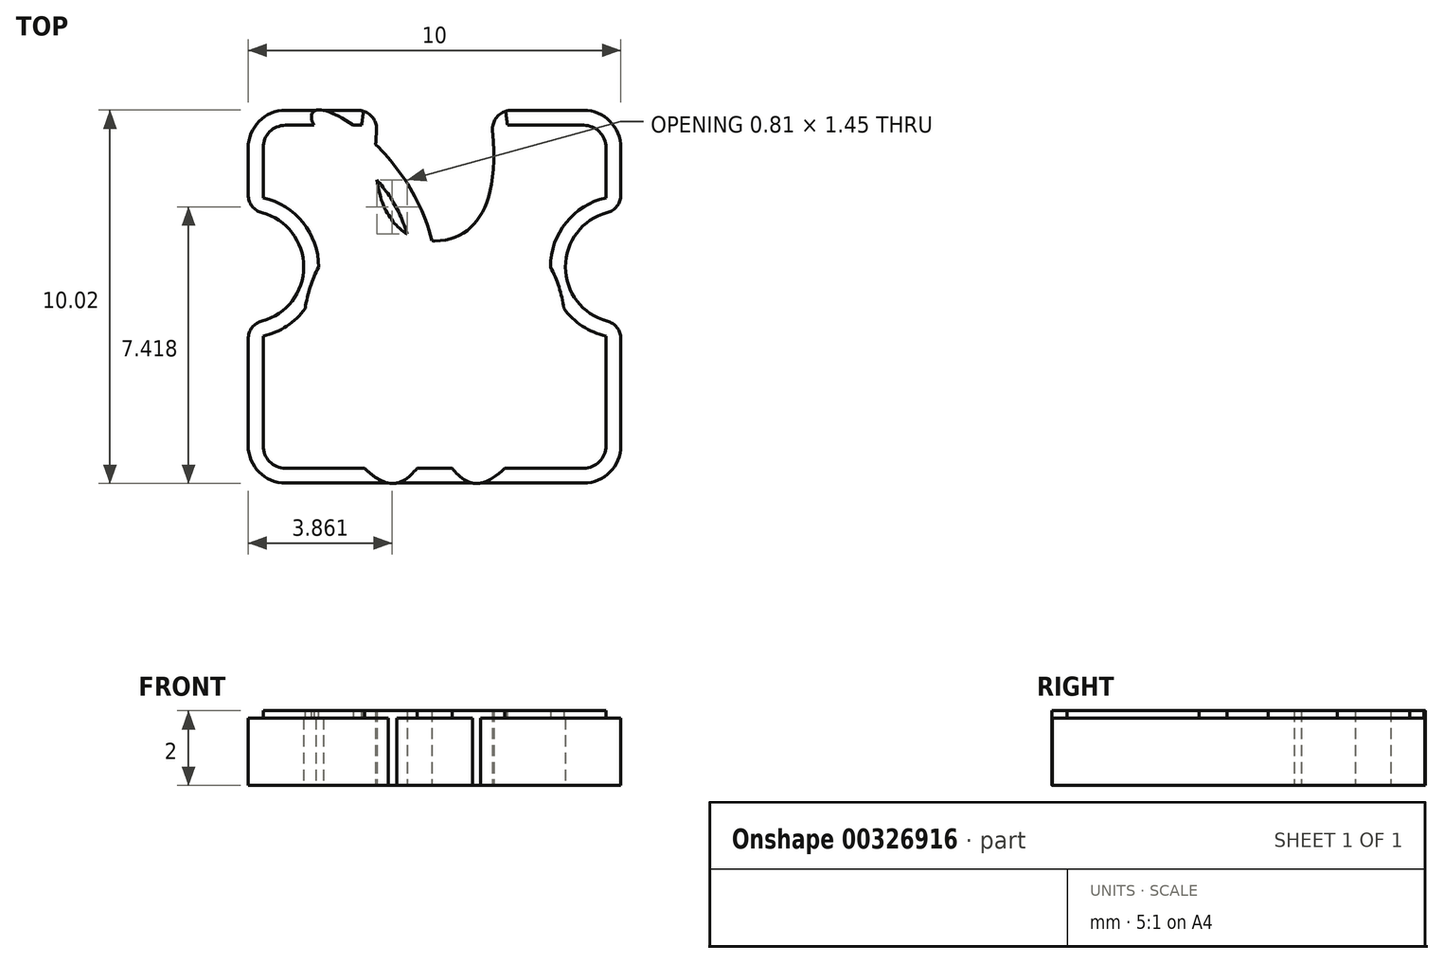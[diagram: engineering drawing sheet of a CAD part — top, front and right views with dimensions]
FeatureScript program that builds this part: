
annotation { "Feature Type Name" : "Feature", "Feature Type Description" : "" }
export const myFeature = defineFeature(function(context is Context, id is Id, definition is map)
    precondition{}
    {
        {
            var Q0;
            Q0=qCreatedBy(makeId("Top.planeOp"),FACE);
            var sketch = newSketch(context, id + "F0", { "sketchPlane" : qUnion([Q0])});
            skLineSegment(sketch, "E0.bottom", {"start": v(5, -5) * mm, "end": v(-5, -5) * mm, "construction": true});
            skLineSegment(sketch, "E0.top", {"start": v(5, 5) * mm, "end": v(-5, 5) * mm, "construction": true});
            skLineSegment(sketch, "E0.left", {"start": v(5, -5) * mm, "end": v(5, 5) * mm, "construction": true});
            skLineSegment(sketch, "E0.right", {"start": v(-5, -5) * mm, "end": v(-5, 5) * mm, "construction": true});
            skPoint(sketch, "E0.middle", {"position": v(0, 0) * mm});
            skLineSegment(sketch, "E1", {"start": v(-4, 5) * mm, "end": v(-2.05, 5) * mm});
            skLineSegment(sketch, "E2", {"start": v(5, 5.2) * mm, "end": v(5, 5) * mm});
            skLineSegment(sketch, "E3", {"start": v(0, -5) * mm, "end": v(-4, -5) * mm});
            skLineSegment(sketch, "E4", {"start": v(-5, 4) * mm, "end": v(-5, 2.73) * mm});
            skLineSegment(sketch, "E5", {"start": v(-5, -1.13) * mm, "end": v(-5, -4) * mm});
            skArc(sketch, "E6", {"start": v(-4.63, -0.65) * mm, "mid": v(-3.5, 0.8) * mm, "end": v(-4.63, 2.25) * mm});
            skLineSegment(sketch, "E7", {"start": v(0, 5) * mm, "end": v(0, -5) * mm});
            skFitSpline(sketch, "E8", {"points": [v(-1.5, 5) * mm, v(-1.1, 2) * mm, v(0, 1.5) * mm], "startDerivative": vector(-1.05, -8.39) * mm, "endDerivative": vector(3.92, 0) * mm});
            skArc(sketch, "E9.filletArc", {"start": v(-1.56, 4.46) * mm, "mid": v(-1.69, 4.84) * mm, "end": v(-2.05, 5) * mm});
            skPoint(sketch, "E10.visualSharp", {"position": v(-5, 5) * mm});
            skArc(sketch, "E10.filletArc", {"start": v(-4, 5) * mm, "mid": v(-4.7, 4.7) * mm, "end": v(-5, 4) * mm});
            skPoint(sketch, "E11.visualSharp", {"position": v(-5, -5) * mm});
            skArc(sketch, "E11.filletArc", {"start": v(-5, -4) * mm, "mid": v(-4.7, -4.7) * mm, "end": v(-4, -5) * mm});
            skPoint(sketch, "E12.visualSharp", {"position": v(-5, 2.3) * mm});
            skArc(sketch, "E12.filletArc", {"start": v(-5, 2.73) * mm, "mid": v(-4.9, 2.43) * mm, "end": v(-4.63, 2.25) * mm});
            skPoint(sketch, "E13.visualSharp", {"position": v(-5, -0.7) * mm});
            skArc(sketch, "E13.filletArc", {"start": v(-4.63, -0.65) * mm, "mid": v(-4.9, -0.83) * mm, "end": v(-5, -1.13) * mm});
            skSolve(sketch);
        }
        {
            var Q0;
            Q0 = qSketchRegion(id + "F0", true);
            extrude(context, id + "F1", {"entities" : qUnion([Q0]), "depth" : 2 * mm});
        }
        {
            var Q0;
            Q0=makeQuery(id+"F1.opExtrude","SWEPT_BODY",BODY,{"disambiguationData":[OSD([sQuery(id+"F0.wireOp",EDGE,"E1"),sQuery(id+"F0.wireOp",EDGE,"E3"),sQuery(id+"F0.wireOp",EDGE,"E4"),sQuery(id+"F0.wireOp",EDGE,"E5"),sQuery(id+"F0.wireOp",EDGE,"E6"),sQuery(id+"F0.wireOp",EDGE,"E7"),sQuery(id+"F0.wireOp",EDGE,"E8"),sQuery(id+"F0.wireOp",EDGE,"E9.filletArc"),sQuery(id+"F0.wireOp",EDGE,"E10.filletArc"),sQuery(id+"F0.wireOp",EDGE,"E11.filletArc"),sQuery(id+"F0.wireOp",EDGE,"E12.filletArc"),sQuery(id+"F0.wireOp",EDGE,"E13.filletArc")])]});
            var Q1;
            Q1=qCreatedBy(makeId("Right.planeOp"),FACE);
            mirror(context, id + "F2", {"operationType" : NewBodyOperationType.ADD, "entities" : qUnion([Q0]), "mirrorPlane" : qUnion([Q1])});
        }
        {
            var Q0;
            {var subQ0=makeQuery(id+"F1.opExtrude","CAP_FACE",FACE,{"disambiguationData":[OSD([sQuery(id+"F0.wireOp",EDGE,"E1"),sQuery(id+"F0.wireOp",EDGE,"E3"),sQuery(id+"F0.wireOp",EDGE,"E4"),sQuery(id+"F0.wireOp",EDGE,"E5"),sQuery(id+"F0.wireOp",EDGE,"E6"),sQuery(id+"F0.wireOp",EDGE,"E7"),sQuery(id+"F0.wireOp",EDGE,"E8"),sQuery(id+"F0.wireOp",EDGE,"E9.filletArc"),sQuery(id+"F0.wireOp",EDGE,"E10.filletArc"),sQuery(id+"F0.wireOp",EDGE,"E11.filletArc"),sQuery(id+"F0.wireOp",EDGE,"E12.filletArc"),sQuery(id+"F0.wireOp",EDGE,"E13.filletArc")])],"isStart":false});Q0=makeQuery(id+"F2.boolean.opBoolean","MERGE",FACE,{"derivedFrom":[subQ0,makeQuery(id+"F2.opPattern","COPY",FACE,{"derivedFrom":subQ0,"instanceName":"1"})]});}
            var sketch = newSketch(context, id + "F3", { "sketchPlane" : qUnion([Q0])});
            skArc(sketch, "E14.0", {"start": v(-4.6, 2.66) * mm, "mid": v(-3.1, 0.8) * mm, "end": v(-4.6, -1.06) * mm});
            skLineSegment(sketch, "E14.1", {"start": v(-4.6, 4) * mm, "end": v(-4.6, 2.66) * mm});
            skArc(sketch, "E14.2", {"start": v(-4, 4.6) * mm, "mid": v(-4.42, 4.42) * mm, "end": v(-4.6, 4) * mm});
            skLineSegment(sketch, "E14.3", {"start": v(-1.95, 4.6) * mm, "end": v(-4, 4.6) * mm});
            skLineSegment(sketch, "E14.4", {"start": v(4.6, -4) * mm, "end": v(4.6, -1.06) * mm});
            skArc(sketch, "E14.5", {"start": v(4, -4.6) * mm, "mid": v(4.42, -4.42) * mm, "end": v(4.6, -4) * mm});
            skLineSegment(sketch, "E14.6", {"start": v(-4, -4.6) * mm, "end": v(4, -4.6) * mm});
            skArc(sketch, "E14.7", {"start": v(-4.6, -4) * mm, "mid": v(-4.42, -4.42) * mm, "end": v(-4, -4.6) * mm});
            skArc(sketch, "E14.8", {"start": v(4.6, -1.06) * mm, "mid": v(3.1, 0.8) * mm, "end": v(4.6, 2.66) * mm});
            skLineSegment(sketch, "E14.9", {"start": v(4.6, 2.66) * mm, "end": v(4.6, 4) * mm});
            skArc(sketch, "E14.10", {"start": v(4.6, 4) * mm, "mid": v(4.42, 4.42) * mm, "end": v(4, 4.6) * mm});
            skLineSegment(sketch, "E14.11", {"start": v(4, 4.6) * mm, "end": v(1.95, 4.6) * mm});
            skLineSegment(sketch, "E14.12", {"start": v(-4.6, -1.06) * mm, "end": v(-4.6, -4) * mm});
            skFitSpline(sketch, "E14.13", {"points": [v(1.9, 5.05) * mm, v(1.99, 4.33) * mm, v(2.02, 3.47) * mm, v(1.87, 2.62) * mm, v(1.7, 2.19) * mm, v(1.53, 1.9) * mm, v(1.38, 1.7) * mm, v(1.21, 1.53) * mm, v(0.95, 1.33) * mm, v(0.56, 1.15) * mm, v(0.2, 1.1) * mm, v(0, 1.1) * mm]});
            skFitSpline(sketch, "E14.14", {"points": [v(0, 1.1) * mm, v(-0.2, 1.1) * mm, v(-0.56, 1.15) * mm, v(-0.95, 1.33) * mm, v(-1.21, 1.53) * mm, v(-1.38, 1.7) * mm, v(-1.53, 1.9) * mm, v(-1.7, 2.19) * mm, v(-1.87, 2.62) * mm, v(-2.02, 3.47) * mm, v(-1.99, 4.33) * mm, v(-1.9, 5.05) * mm]});
            skSolve(sketch);
        }
        {
            var Q0;
            Q0=makeQuery(id+"F3.imprint","IMPRINT",FACE,{"disambiguationData":[TD([[makeQuery(id+"F3.imprint","IMPRINT",EDGE,{"derivedFrom":sQuery(id+"F3.wireOp",EDGE,"E14.0")}),1.0]])]});
            extrude(context, id + "F4", {"entities" : qUnion([Q0]), "operationType" : NewBodyOperationType.REMOVE, "oppositeDirection" : true, "depth" : .2 * mm});
        }
        {
            var Q0;
            Q0=qCreatedBy(makeId("Top.planeOp"),FACE);
            var sketch = newSketch(context, id + "F5", { "sketchPlane" : qUnion([Q0])});
            skLineSegment(sketch, "E15.bottom", {"start": v(3.5, -5) * mm, "end": v(-3.5, -5) * mm, "construction": true});
            skLineSegment(sketch, "E15.top", {"start": v(3.5, 5) * mm, "end": v(-3.5, 5) * mm, "construction": true});
            skLineSegment(sketch, "E15.left", {"start": v(3.5, -5) * mm, "end": v(3.5, 5) * mm, "construction": true});
            skLineSegment(sketch, "E15.right", {"start": v(-3.5, -5) * mm, "end": v(-3.5, 5) * mm, "construction": true});
            skPoint(sketch, "E15.middle", {"position": v(0, 0) * mm});
            skLineSegment(sketch, "E16", {"start": v(-3.5, 2) * mm, "end": v(3.5, 2) * mm, "construction": true});
            skFitSpline(sketch, "E17", {"points": [v(0, 1.15) * mm, v(-0.46, 1.27) * mm, v(-1.6, 2) * mm, v(-3.5, -0.66) * mm, v(-1.24, -5) * mm, v(-0.36, -4.45) * mm, v(0, -4.15) * mm], "startDerivative": vector(-7.66, 0) * mm, "endDerivative": vector(5.7, 0) * mm});
            skLineSegment(sketch, "E18", {"start": v(0, 1.15) * mm, "end": v(0, -4.15) * mm});
            skLineSegment(sketch, "E19", {"start": v(0, 1.15) * mm, "end": v(-0.6, 1.15) * mm, "construction": true});
            skFitSpline(sketch, "E20", {"points": [v(-0.6, 1.15) * mm, v(-3.2, 4.54) * mm, v(-3.19, 5) * mm, v(0, 1.15) * mm], "startDerivative": vector(-3.15, 16.75) * mm, "endDerivative": vector(2.71, -16.5) * mm});
            skSolve(sketch);
        }
        {
            var Q0;
            {var subQ1=sQuery(id+"F5.wireOp",EDGE,"E18");Q0=makeQuery(id+"F5.imprint","IMPRINT",FACE,{"disambiguationData":[TD([[makeQuery(id+"F5.imprint","IMPRINT",EDGE,{"derivedFrom":subQ1}),-1.0]])]});}
            extrude(context, id + "F6", {"entities" : qUnion([Q0]), "depth" : 2 * mm});
        }
        {
            var Q0;
            Q0=makeQuery(id+"F6.opExtrude","SWEPT_BODY",BODY,{"disambiguationData":[OSD([sQuery(id+"F5.wireOp",EDGE,"E17"),sQuery(id+"F5.wireOp",EDGE,"E18")])]});
            var Q1;
            Q1=qCreatedBy(makeId("Right.planeOp"),FACE);
            mirror(context, id + "F7", {"operationType" : NewBodyOperationType.ADD, "entities" : qUnion([Q0]), "mirrorPlane" : qUnion([Q1])});
        }
        {
            var Q0;
            {var subQ0=sQuery(id+"F5.wireOp",EDGE,"E20");var subQ1=sQuery(id+"F5.wireOp",EDGE,"E17");var subQ3=makeQuery(id+"F5.imprint","INTERSECT",VERTEX,{"derivedFrom":[subQ1,subQ0]});Q0=makeQuery(id+"F5.imprint","IMPRINT",FACE,{"disambiguationData":[TD([[makeQuery(id+"F5.imprint","IMPRINT",EDGE,{"disambiguationData":[TD([[subQ3,1.0]])],"derivedFrom":subQ1}),-1.0]])]});}
            extrude(context, id + "F8", {"entities" : qUnion([Q0]), "operationType" : NewBodyOperationType.ADD, "depth" : 2 * mm});
        }
    });
